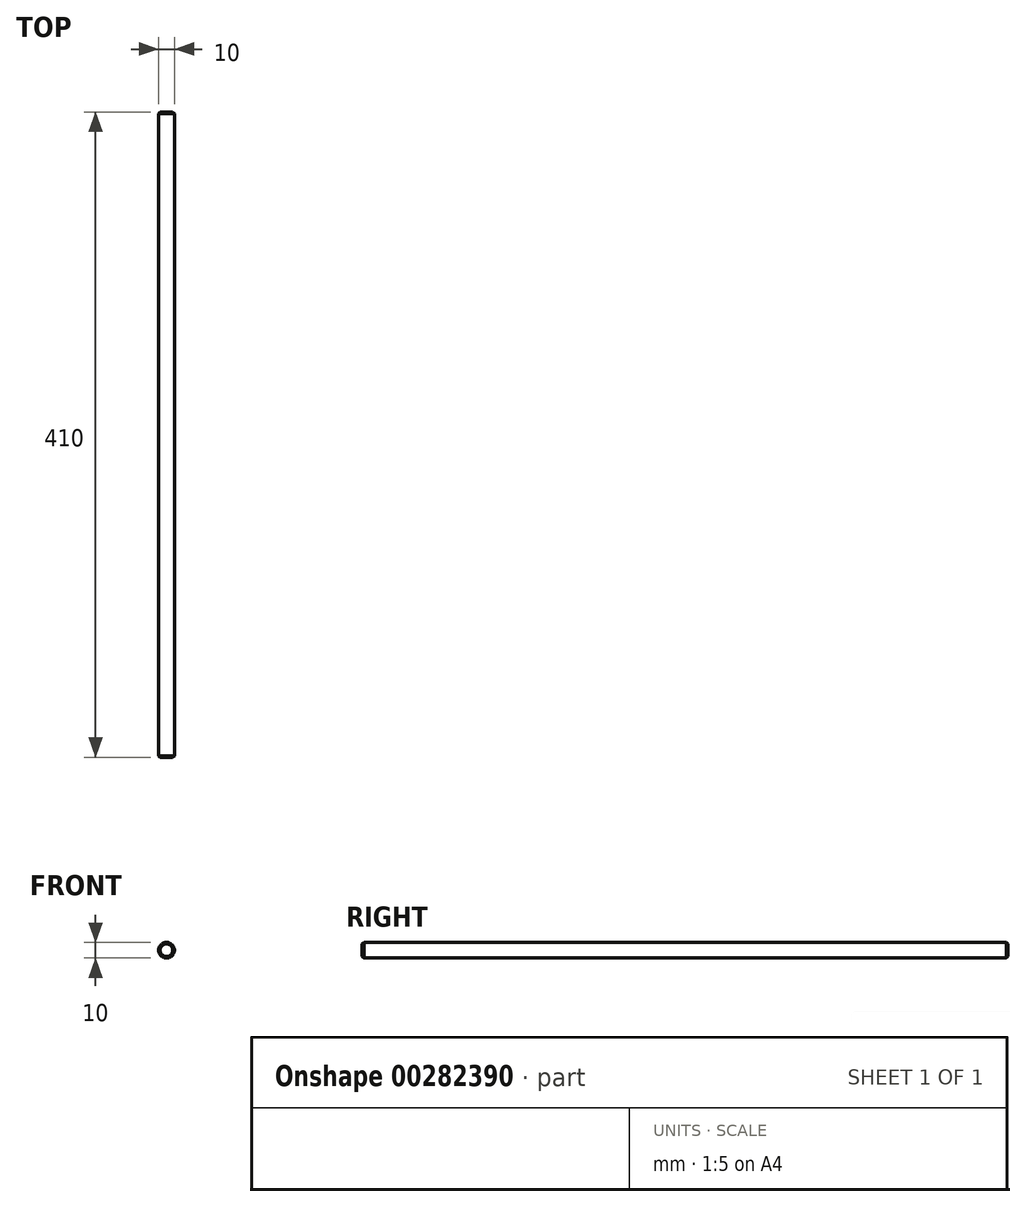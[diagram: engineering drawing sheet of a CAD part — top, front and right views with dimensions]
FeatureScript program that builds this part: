
annotation { "Feature Type Name" : "Feature", "Feature Type Description" : "" }
export const myFeature = defineFeature(function(context is Context, id is Id, definition is map)
    precondition{}
    {
        {
            var Q0;
            Q0=qCreatedBy(makeId("Front.planeOp"),FACE);
            var sketch = newSketch(context, id + "F0", { "sketchPlane" : qUnion([Q0])});
            skCircle(sketch, "E0", {"center": v(0, 0) * mm, "radius": 5 * mm});
            skSolve(sketch);
        }
        {
            var Q0;
            Q0=qSketchRegion(id+"F0",true);
            extrude(context, id + "F1", {"entities" : qUnion([Q0]), "depth" : 410 * mm});
        }
        {
            var Q0;
            Q0=makeQuery(id+"F1.opExtrude","CAP_EDGE",EDGE,{"disambiguationData":[OSD([sQuery(id+"F0.wireOp",EDGE,"E0")])],"isStart":false});
            var Q1;
            Q1=makeQuery(id+"F1.opExtrude","CAP_EDGE",EDGE,{"disambiguationData":[OSD([sQuery(id+"F0.wireOp",EDGE,"E0")])],"isStart":true});
            chamfer(context, id + "F2", {"entities" : qUnion([Q0, Q1]), "width" : 1 * mm, "tangentPropagation" : true});
        }
    });
